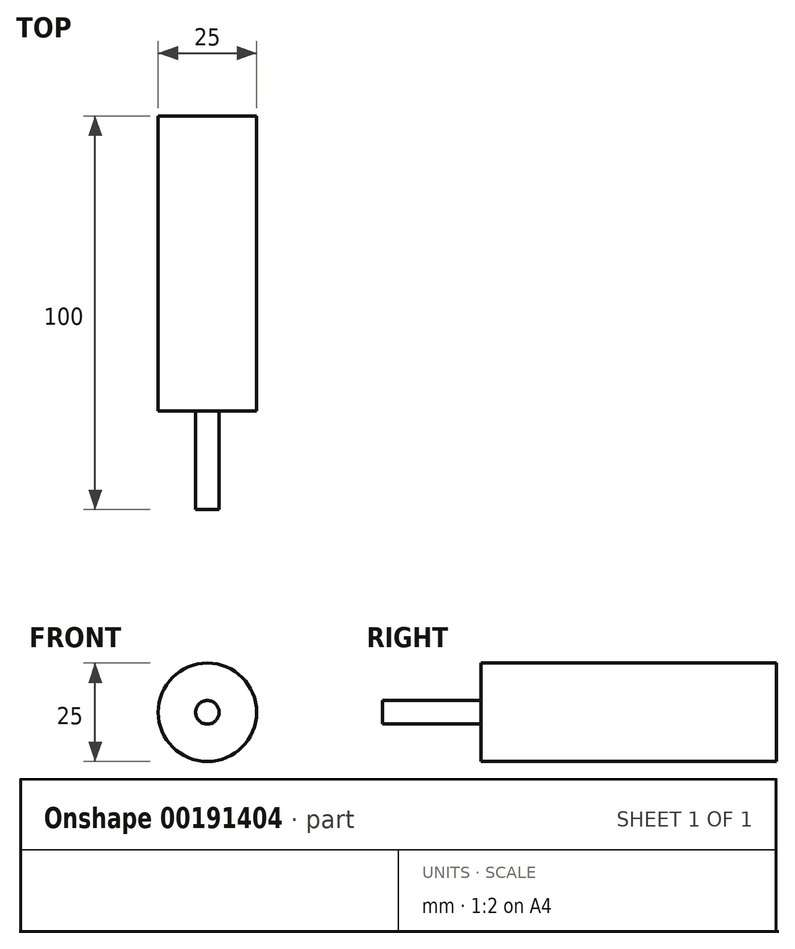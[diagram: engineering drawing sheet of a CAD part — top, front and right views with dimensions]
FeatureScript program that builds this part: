
annotation { "Feature Type Name" : "Feature", "Feature Type Description" : "" }
export const myFeature = defineFeature(function(context is Context, id is Id, definition is map)
    precondition{}
    {
        {
            var Q0;
            Q0=qCreatedBy(makeId("Front.planeOp"),FACE);
            var sketch = newSketch(context, id + "F0", { "sketchPlane" : qUnion([Q0])});
            skCircle(sketch, "E0", {"center": v(0, 0) * mm, "radius": 12.5 * mm});
            skSolve(sketch);
        }
        {
            var Q0;
            Q0=makeQuery(id+"F0.imprint","IMPRINT",FACE,{"disambiguationData":[TD([[makeQuery(id+"F0.imprint","IMPRINT",EDGE,{"derivedFrom":sQuery(id+"F0.wireOp",EDGE,"E0")}),1.0]])]});
            extrude(context, id + "F1", {"entities" : qUnion([Q0]), "depth" : 75 * mm});
        }
        {
            var Q0;
            Q0=makeQuery(id+"F1.opExtrude","CAP_FACE",FACE,{"disambiguationData":[OSD([sQuery(id+"F0.wireOp",EDGE,"E0")])],"isStart":false});
            var sketch = newSketch(context, id + "F2", { "sketchPlane" : qUnion([Q0])});
            skPoint(sketch, "E1", {"position": v(0, 0) * mm});
            skCircle(sketch, "E2", {"center": v(0, 0) * mm, "radius": 3 * mm});
            skSolve(sketch);
        }
        {
            var Q0;
            Q0=makeQuery(id+"F2.imprint","IMPRINT",FACE,{"disambiguationData":[TD([[makeQuery(id+"F2.imprint","IMPRINT",EDGE,{"derivedFrom":sQuery(id+"F2.wireOp",EDGE,"E2")}),1.0]])]});
            extrude(context, id + "F3", {"entities" : qUnion([Q0]), "operationType" : NewBodyOperationType.ADD, "depth" : 25 * mm});
        }
    });
